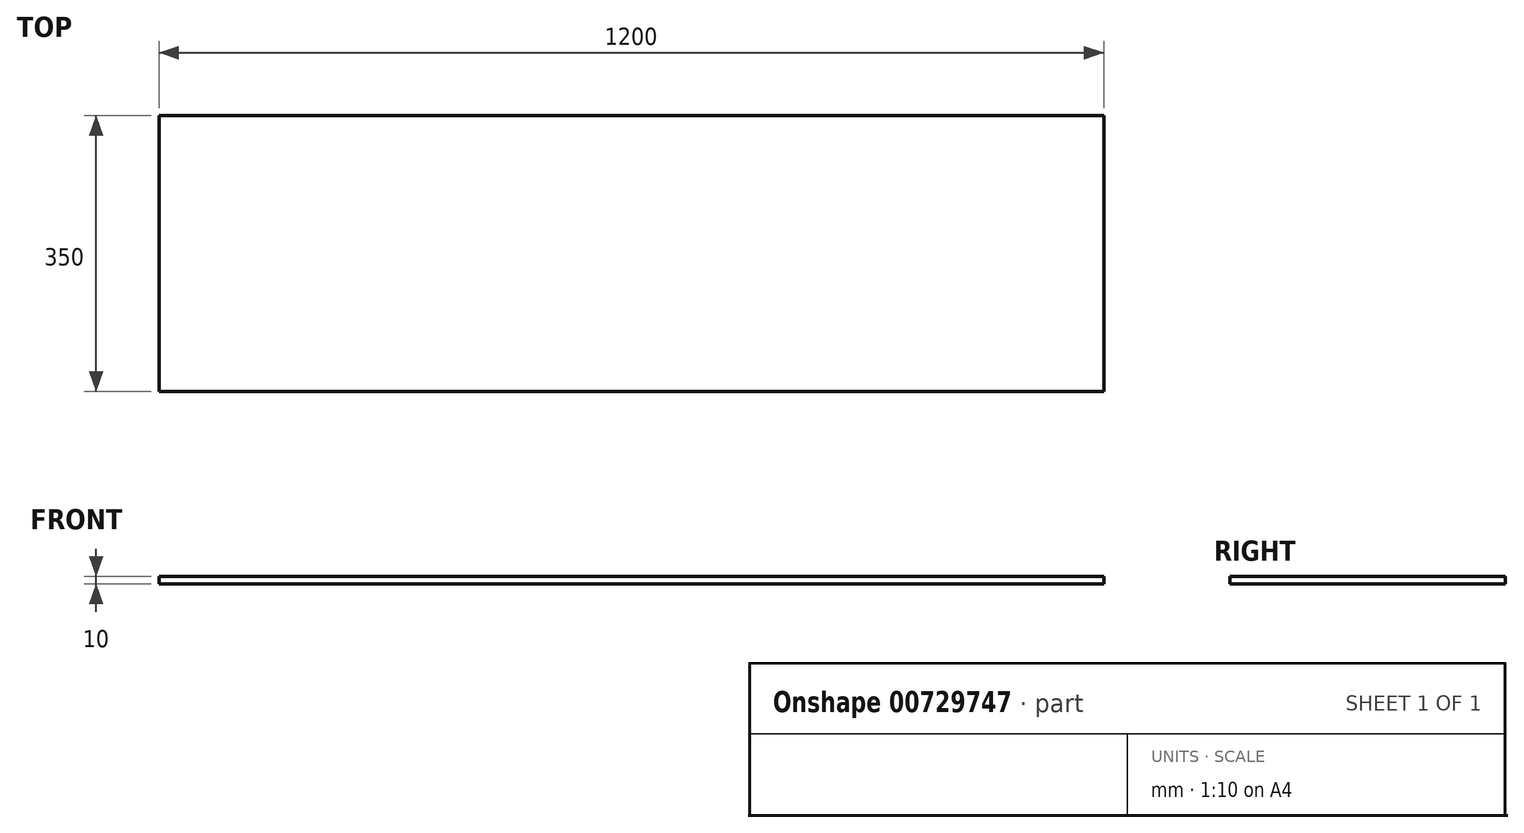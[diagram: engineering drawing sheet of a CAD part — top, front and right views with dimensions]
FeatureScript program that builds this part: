
annotation { "Feature Type Name" : "Feature", "Feature Type Description" : "" }
export const myFeature = defineFeature(function(context is Context, id is Id, definition is map)
    precondition{}
    {
        {
            var Q0;
            Q0=qCreatedBy(makeId("Top.planeOp"),FACE);
            var sketch = newSketch(context, id + "F0", { "sketchPlane" : qUnion([Q0])});
            skLineSegment(sketch, "E0.bottom", {"start": v(-652.86, 170.52) * mm, "end": v(547.14, 170.52) * mm});
            skLineSegment(sketch, "E0.top", {"start": v(-652.86, -179.48) * mm, "end": v(547.14, -179.48) * mm});
            skLineSegment(sketch, "E0.left", {"start": v(-652.86, 170.52) * mm, "end": v(-652.86, -179.48) * mm});
            skLineSegment(sketch, "E0.right", {"start": v(547.14, 170.52) * mm, "end": v(547.14, -179.48) * mm});
            skSolve(sketch);
        }
        {
            var Q0;
            Q0=makeQuery(id+"F0.imprint","IMPRINT",FACE,{"disambiguationData":[TD([[makeQuery(id+"F0.imprint","IMPRINT",EDGE,{"derivedFrom":sQuery(id+"F0.wireOp",EDGE,"E0.bottom")}),-1.0]])]});
            extrude(context, id + "F1", {"entities" : qUnion([Q0]), "depth" : 10 * mm, "offsetDistance" : 25 * mm});
        }
    });
